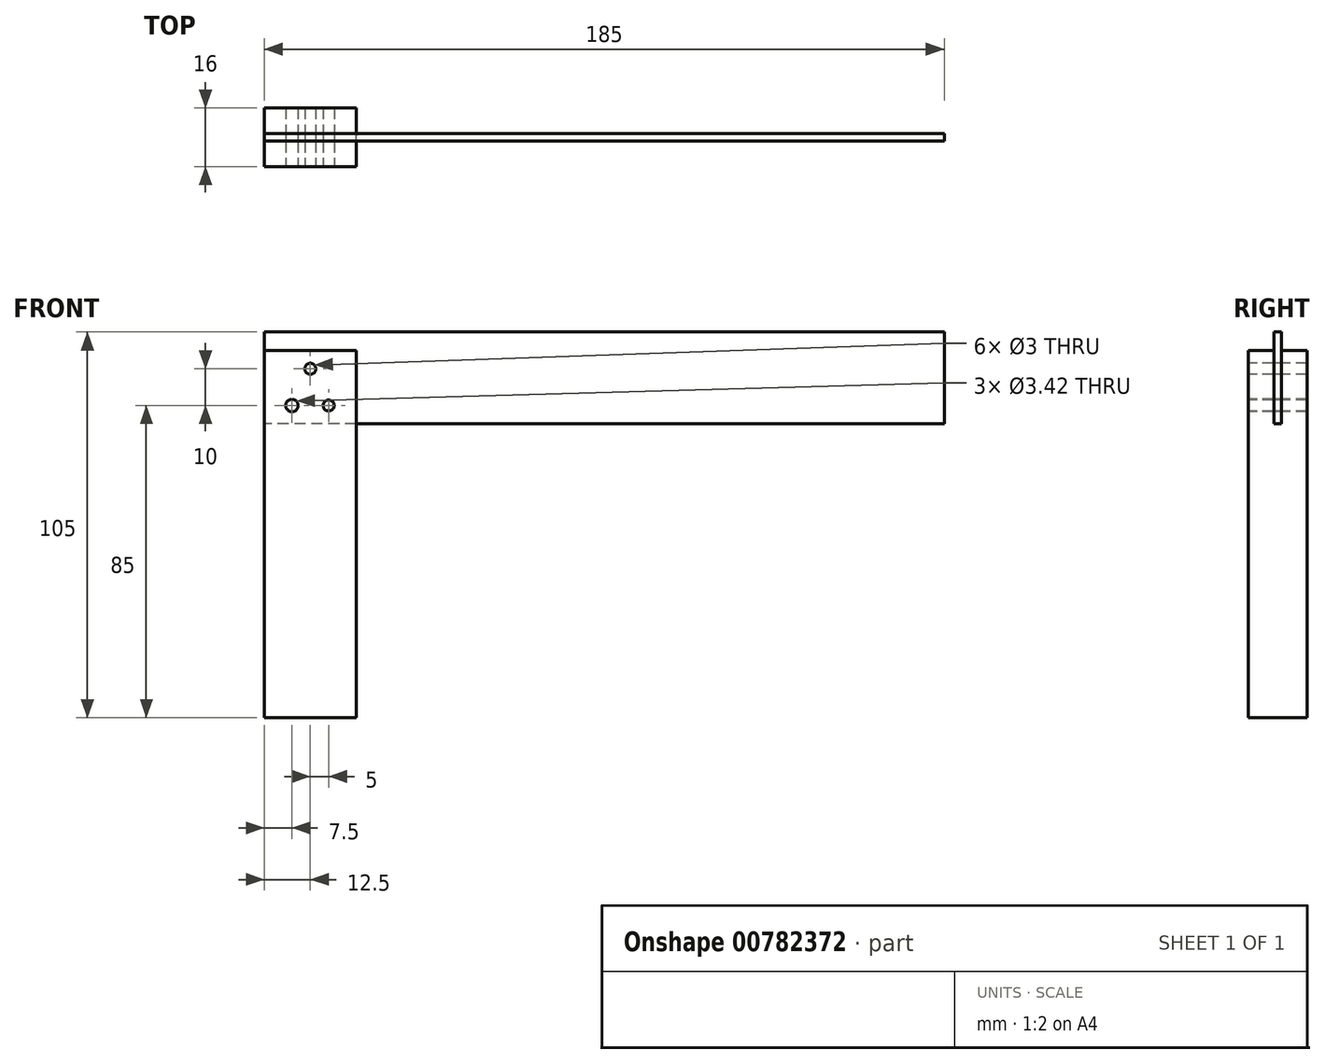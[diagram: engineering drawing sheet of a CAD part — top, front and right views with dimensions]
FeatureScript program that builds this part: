
annotation { "Feature Type Name" : "Feature", "Feature Type Description" : "" }
export const myFeature = defineFeature(function(context is Context, id is Id, definition is map)
    precondition{}
    {
        {
            var Q0;
            Q0=qCreatedBy(makeId("Front.planeOp"),FACE);
            var sketch = newSketch(context, id + "F0", { "sketchPlane" : qUnion([Q0])});
            skLineSegment(sketch, "E0.bottom", {"start": v(0, 0) * mm, "end": v(25, 0) * mm});
            skLineSegment(sketch, "E0.top", {"start": v(0, 100) * mm, "end": v(25, 100) * mm});
            skLineSegment(sketch, "E0.left", {"start": v(0, 0) * mm, "end": v(0, 100) * mm});
            skLineSegment(sketch, "E0.right", {"start": v(25, 0) * mm, "end": v(25, 100) * mm});
            skSolve(sketch);
        }
        {
            var Q0;
            Q0=makeQuery(id+"F0.imprint","IMPRINT",FACE,{"disambiguationData":[TD([[makeQuery(id+"F0.imprint","IMPRINT",EDGE,{"derivedFrom":sQuery(id+"F0.wireOp",EDGE,"E0.bottom")}),1.0]])]});
            extrude(context, id + "F1", {"entities" : qUnion([Q0]), "oppositeDirection" : true, "depth" : 16 * mm, "offsetDistance" : 25 * mm});
        }
        {
            var Q0;
            Q0=makeQuery(id+"F1.opExtrude","SWEPT_FACE",FACE,{"disambiguationData":[OSD([sQuery(id+"F0.wireOp",EDGE,"E0.right")])]});
            var sketch = newSketch(context, id + "F2", { "sketchPlane" : qUnion([Q0])});
            skLineSegment(sketch, "E1.bottom", {"start": v(7, 100) * mm, "end": v(9, 100) * mm});
            skLineSegment(sketch, "E1.top", {"start": v(7, 80) * mm, "end": v(9, 80) * mm});
            skLineSegment(sketch, "E1.left", {"start": v(7, 100) * mm, "end": v(7, 80) * mm});
            skLineSegment(sketch, "E1.right", {"start": v(9, 100) * mm, "end": v(9, 80) * mm});
            skSolve(sketch);
        }
        {
            var Q0;
            Q0 = qSketchRegion(id + "F2", true);
            var Q1;
            Q1=makeQuery(id+"F1.opExtrude","SWEPT_FACE",FACE,{"disambiguationData":[OSD([sQuery(id+"F0.wireOp",EDGE,"E0.left")])]});
            extrude(context, id + "F3", {"entities" : qUnion([Q0]), "operationType" : NewBodyOperationType.REMOVE, "endBound" : BoundingType.UP_TO_SURFACE, "oppositeDirection" : true, "depth" : 25 * mm, "endBoundEntityFace" : qUnion([Q1]), "offsetDistance" : 25 * mm});
        }
        {
            var Q0;
            Q0=makeQuery(id+"F1.opExtrude","SWEPT_FACE",FACE,{"disambiguationData":[OSD([sQuery(id+"F0.wireOp",EDGE,"E0.left")])]});
            var sketch = newSketch(context, id + "F4", { "sketchPlane" : qUnion([Q0])});
            skLineSegment(sketch, "E2.bottom", {"start": v(-9, 80) * mm, "end": v(-7, 80) * mm});
            skLineSegment(sketch, "E2.top", {"start": v(-9, 105) * mm, "end": v(-7, 105) * mm});
            skLineSegment(sketch, "E2.left", {"start": v(-9, 80) * mm, "end": v(-9, 105) * mm});
            skLineSegment(sketch, "E2.right", {"start": v(-7, 80) * mm, "end": v(-7, 105) * mm});
            skSolve(sketch);
        }
        {
            var Q0;
            {var subQ10=sQuery(id+"F4.wireOp",EDGE,"E2.bottom");Q0=makeQuery(id+"F4.imprint","IMPRINT",FACE,{"disambiguationData":[TD([[makeQuery(id+"F4.imprint","IMPRINT",EDGE,{"derivedFrom":subQ10}),1.0]])]});}
            extrude(context, id + "F5", {"entities" : qUnion([Q0]), "oppositeDirection" : true, "depth" : 185 * mm, "offsetDistance" : 25 * mm});
        }
        {
            var Q0;
            Q0=makeQuery(id+"F1.opExtrude","CAP_FACE",FACE,{"disambiguationData":[OSD([sQuery(id+"F0.wireOp",EDGE,"E0.bottom"),sQuery(id+"F0.wireOp",EDGE,"E0.top"),sQuery(id+"F0.wireOp",EDGE,"E0.left"),sQuery(id+"F0.wireOp",EDGE,"E0.right")])],"isStart":true});
            var sketch = newSketch(context, id + "F6", { "sketchPlane" : qUnion([Q0])});
            skCircle(sketch, "E3", {"center": v(12.5, 95) * mm, "radius": 1.5 * mm});
            skCircle(sketch, "E4", {"center": v(7.5, 85) * mm, "radius": 1.7 * mm});
            skCircle(sketch, "E5", {"center": v(17.5, 85) * mm, "radius": 1.5 * mm});
            skSolve(sketch);
        }
        {
            var Q0;
            Q0=makeQuery(id+"F6.imprint","IMPRINT",FACE,{"disambiguationData":[TD([[makeQuery(id+"F6.imprint","IMPRINT",EDGE,{"derivedFrom":sQuery(id+"F6.wireOp",EDGE,"E3")}),1.0]])]});
            var Q1;
            Q1=makeQuery(id+"F6.imprint","IMPRINT",FACE,{"disambiguationData":[TD([[makeQuery(id+"F6.imprint","IMPRINT",EDGE,{"derivedFrom":sQuery(id+"F6.wireOp",EDGE,"E5")}),1.0]])]});
            var Q2;
            Q2=makeQuery(id+"F6.imprint","IMPRINT",FACE,{"disambiguationData":[TD([[makeQuery(id+"F6.imprint","IMPRINT",EDGE,{"derivedFrom":sQuery(id+"F6.wireOp",EDGE,"E4")}),1.0]])]});
            var Q3;
            Q3=makeQuery(id+"F1.opExtrude","CAP_FACE",FACE,{"disambiguationData":[OSD([sQuery(id+"F0.wireOp",EDGE,"E0.bottom"),sQuery(id+"F0.wireOp",EDGE,"E0.top"),sQuery(id+"F0.wireOp",EDGE,"E0.left"),sQuery(id+"F0.wireOp",EDGE,"E0.right")])],"isStart":false});
            extrude(context, id + "F7", {"entities" : qUnion([Q0, Q1, Q2]), "operationType" : NewBodyOperationType.REMOVE, "endBound" : BoundingType.UP_TO_SURFACE, "oppositeDirection" : true, "depth" : 25 * mm, "endBoundEntityFace" : qUnion([Q3]), "offsetDistance" : 25 * mm});
        }
        {
            var Q0;
            Q0=makeQuery(id+"F1.opExtrude","CAP_FACE",FACE,{"disambiguationData":[OSD([sQuery(id+"F0.wireOp",EDGE,"E0.bottom"),sQuery(id+"F0.wireOp",EDGE,"E0.top"),sQuery(id+"F0.wireOp",EDGE,"E0.left"),sQuery(id+"F0.wireOp",EDGE,"E0.right")])],"isStart":true});
            var sketch = newSketch(context, id + "F8", { "sketchPlane" : qUnion([Q0])});
            skCircle(sketch, "E6", {"center": v(12.5, 95) * mm, "radius": 1.5 * mm});
            skCircle(sketch, "E7", {"center": v(7.5, 85) * mm, "radius": 1.7 * mm});
            skCircle(sketch, "E8", {"center": v(17.5, 85) * mm, "radius": 1.5 * mm});
            skSolve(sketch);
        }
        {
            var Q0;
            Q0=makeQuery(id+"F8.imprint","IMPRINT",FACE,{"disambiguationData":[TD([[makeQuery(id+"F8.imprint","IMPRINT",EDGE,{"derivedFrom":sQuery(id+"F8.wireOp",EDGE,"E6")}),1.0]])]});
            var Q1;
            Q1=makeQuery(id+"F8.imprint","IMPRINT",FACE,{"disambiguationData":[TD([[makeQuery(id+"F8.imprint","IMPRINT",EDGE,{"derivedFrom":sQuery(id+"F8.wireOp",EDGE,"E7")}),1.0]])]});
            var Q2;
            Q2=makeQuery(id+"F8.imprint","IMPRINT",FACE,{"disambiguationData":[TD([[makeQuery(id+"F8.imprint","IMPRINT",EDGE,{"derivedFrom":sQuery(id+"F8.wireOp",EDGE,"E8")}),1.0]])]});
            var Q3;
            Q3=makeQuery(id+"F1.opExtrude","CAP_FACE",FACE,{"disambiguationData":[OSD([sQuery(id+"F0.wireOp",EDGE,"E0.bottom"),sQuery(id+"F0.wireOp",EDGE,"E0.top"),sQuery(id+"F0.wireOp",EDGE,"E0.left"),sQuery(id+"F0.wireOp",EDGE,"E0.right")])],"isStart":false});
            extrude(context, id + "F9", {"entities" : qUnion([Q0, Q1, Q2]), "endBound" : BoundingType.UP_TO_SURFACE, "oppositeDirection" : true, "depth" : 25 * mm, "endBoundEntityFace" : qUnion([Q3]), "offsetDistance" : 25 * mm});
        }
    });
